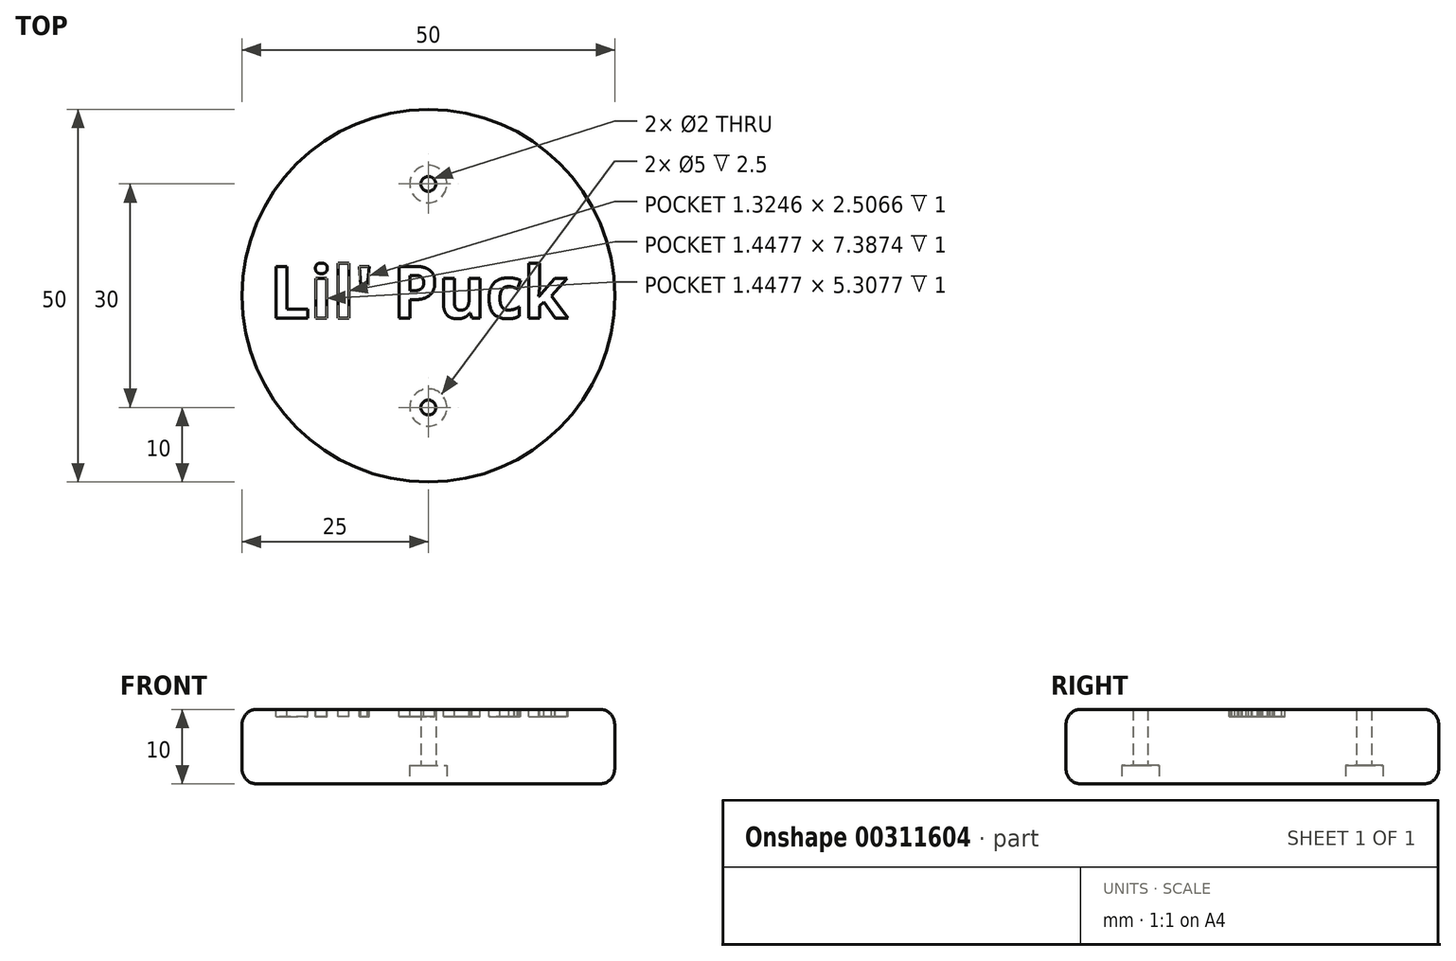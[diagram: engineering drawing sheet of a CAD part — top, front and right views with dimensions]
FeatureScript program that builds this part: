
annotation { "Feature Type Name" : "Feature", "Feature Type Description" : "" }
export const myFeature = defineFeature(function(context is Context, id is Id, definition is map)
    precondition{}
    {
        {
            var Q0;
            Q0=qCreatedBy(makeId("Top.planeOp"),FACE);
            var sketch = newSketch(context, id + "F0", { "sketchPlane" : qUnion([Q0])});
            skCircle(sketch, "E0", {"center": v(0, 0) * mm, "radius": 25 * mm});
            skSolve(sketch);
        }
        {
            var Q0;
            Q0=qSketchRegion(id+"F0",true);
            extrude(context, id + "F1", {"entities" : qUnion([Q0]), "depth" : 10 * mm});
        }
        {
            var Q0;
            Q0=makeQuery(id+"F1.opExtrude","CAP_FACE",FACE,{"disambiguationData":[OSD([sQuery(id+"F0.wireOp",EDGE,"E0")])],"isStart":false});
            var sketch = newSketch(context, id + "F2", { "sketchPlane" : qUnion([Q0])});
            skText(sketch, "E1", { "text": "Lil\' Puck", "fontName": "OpenSans-Bold.ttf"});
            const initialGuessF2  = {"E1": [-0.02134, -0.003, 1, 0, 0.007]};
            skSetInitialGuess(sketch, initialGuessF2);
            skSolve(sketch);
        }
        {
            var Q0;
            Q0=qSketchRegion(id+"F2",true);
            extrude(context, id + "F3", {"entities" : qUnion([Q0]), "operationType" : NewBodyOperationType.REMOVE, "oppositeDirection" : true, "depth" : 1 * mm});
        }
        {
            var Q0;
            Q0=makeQuery(id+"F1.opExtrude","CAP_EDGE",EDGE,{"disambiguationData":[OSD([sQuery(id+"F0.wireOp",EDGE,"E0")])],"isStart":false});
            var Q1;
            Q1=makeQuery(id+"F1.opExtrude","CAP_EDGE",EDGE,{"disambiguationData":[OSD([sQuery(id+"F0.wireOp",EDGE,"E0")])],"isStart":true});
            fillet(context, id + "F4", {"entities" : qUnion([Q0, Q1]), "radius" : 2 * mm, "tangentPropagation" : true, "allowEdgeOverflow" : false});
        }
        {
            var Q0;
            Q0=makeQuery(id+"F1.opExtrude","CAP_FACE",FACE,{"disambiguationData":[OSD([sQuery(id+"F0.wireOp",EDGE,"E0")])],"isStart":true});
            var sketch = newSketch(context, id + "F5", { "sketchPlane" : qUnion([Q0])});
            skPoint(sketch, "E2", {"position": v(0, 15) * mm});
            skPoint(sketch, "E3", {"position": v(0, -15) * mm});
            skSolve(sketch);
        }
        {
            var Q0;
            Q0=sQuery(id+"F5.wireOp",VERTEX,"E2");
            var Q1;
            Q1=sQuery(id+"F5.wireOp",VERTEX,"E3");
            var Q2;
            Q2=makeQuery(id+"F1.opExtrude","SWEPT_BODY",BODY,{"disambiguationData":[OSD([sQuery(id+"F0.wireOp",EDGE,"E0")])]});
            hole(context, id + "F6", {"style" : HoleStyle.C_BORE, "endStyle" : HoleEndStyle.THROUGH, "holeDiameter" : 2 * mm, "cBoreDiameter" : 5 * mm, "cBoreDepth" : 2.5 * mm, "startFromSketch" : true, "locations" : qUnion([Q0, Q1]), "scope" : qUnion([Q2]), "isTappedThrough" : true});
        }
    });
